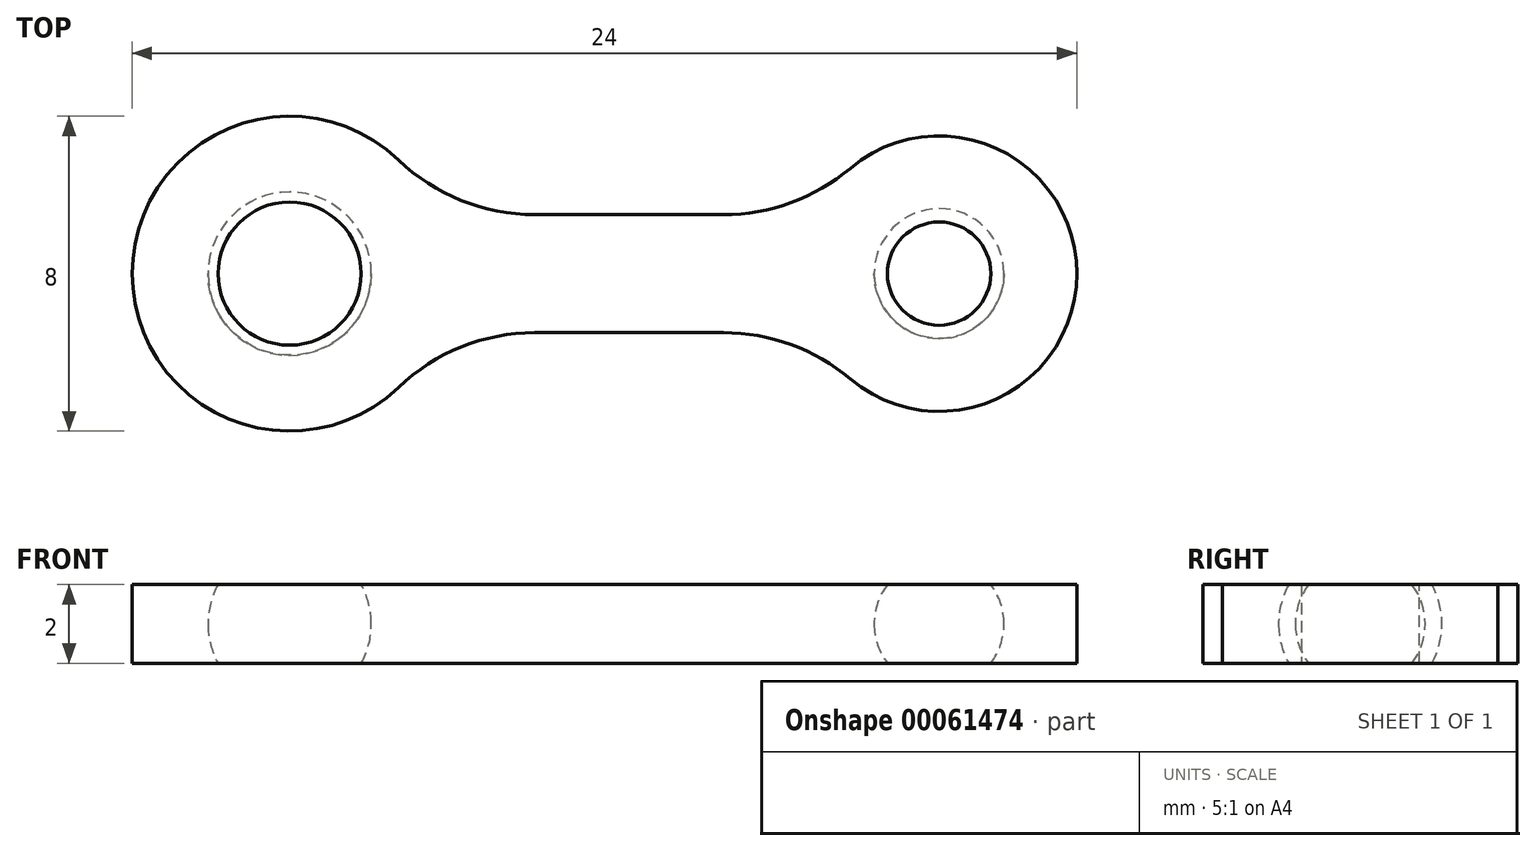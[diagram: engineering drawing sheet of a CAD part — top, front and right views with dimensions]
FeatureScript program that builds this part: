
annotation { "Feature Type Name" : "Feature", "Feature Type Description" : "" }
export const myFeature = defineFeature(function(context is Context, id is Id, definition is map)
    precondition{}
    {
        {
            var Q0;
            Q0=qCreatedBy(makeId("Top.planeOp"),FACE);
            var sketch = newSketch(context, id + "F0", { "sketchPlane" : qUnion([Q0])});
            skLineSegment(sketch, "E0.rect.bottom", {"start": v(5.09, -1.5) * mm, "end": v(-4.54, -1.5) * mm});
            skLineSegment(sketch, "E0.rect.top", {"start": v(5.09, 1.5) * mm, "end": v(-4.54, 1.5) * mm});
            skPoint(sketch, "E0.rect.middle", {"position": v(0, 0) * mm});
            skArc(sketch, "E1", {"start": v(-4.54, 1.5) * mm, "mid": v(-12.25, 0) * mm, "end": v(-4.54, -1.5) * mm});
            skArc(sketch, "E2", {"start": v(5.09, -1.5) * mm, "mid": v(11.75, 0) * mm, "end": v(5.09, 1.5) * mm});
            skPoint(sketch, "E3.orphan", {"position": v(-8.25, 1.5) * mm});
            skPoint(sketch, "E4.orphan", {"position": v(-8.25, -1.5) * mm});
            skPoint(sketch, "E5.orphan", {"position": v(8.25, 1.5) * mm});
            skPoint(sketch, "E6.orphan", {"position": v(8.25, -1.5) * mm});
            skArc(sketch, "E7", {"start": v(-10.33, 0) * mm, "mid": v(-8.25, -2.08) * mm, "end": v(-6.17, 0) * mm});
            skArc(sketch, "E8", {"start": v(6.6, 0) * mm, "mid": v(8.25, -1.65) * mm, "end": v(9.9, 0) * mm});
            skLineSegment(sketch, "E9", {"start": v(-10.33, 0) * mm, "end": v(-6.17, 0) * mm});
            skLineSegment(sketch, "E10", {"start": v(6.6, 0) * mm, "end": v(9.9, 0) * mm});
            skLineSegment(sketch, "E11", {"start": v(-18.85, 0) * mm, "end": v(25.97, 0) * mm, "construction": true});
            skPoint(sketch, "E11.endSnap0", {"position": v(-12.25, 0) * mm});
            skSolve(sketch);
        }
        {
            var Q0;
            Q0=makeQuery(id+"F0.imprint","IMPRINT",FACE,{"disambiguationData":[TD([[makeQuery(id+"F0.imprint","IMPRINT",EDGE,{"derivedFrom":sQuery(id+"F0.wireOp",EDGE,"E0.rect.bottom")}),-1.0]])]});
            var Q1;
            Q1=makeQuery(id+"F0.imprint","IMPRINT",FACE,{"disambiguationData":[TD([[makeQuery(id+"F0.imprint","IMPRINT",EDGE,{"derivedFrom":sQuery(id+"F0.wireOp",EDGE,"E7")}),1.0]])]});
            var Q2;
            Q2=makeQuery(id+"F0.imprint","IMPRINT",FACE,{"disambiguationData":[TD([[makeQuery(id+"F0.imprint","IMPRINT",EDGE,{"derivedFrom":sQuery(id+"F0.wireOp",EDGE,"E8")}),1.0]])]});
            extrude(context, id + "F1", {"entities" : qUnion([Q0, Q1, Q2]), "endBound" : BoundingType.SYMMETRIC, "depth" : 2 * mm});
        }
        {
            var Q0;
            Q0=makeQuery(id+"F0.imprint","IMPRINT",FACE,{"disambiguationData":[TD([[makeQuery(id+"F0.imprint","IMPRINT",EDGE,{"derivedFrom":sQuery(id+"F0.wireOp",EDGE,"E7")}),1.0]])]});
            var Q1;
            Q1=makeQuery(id+"F0.imprint","IMPRINT",FACE,{"disambiguationData":[TD([[makeQuery(id+"F0.imprint","IMPRINT",EDGE,{"derivedFrom":sQuery(id+"F0.wireOp",EDGE,"E8")}),1.0]])]});
            var Q2;
            Q2=sQuery(id+"F0.wireOp",EDGE,"E11");
            revolve(context, id + "F2", {"operationType" : NewBodyOperationType.REMOVE, "entities" : qUnion([Q0, Q1]), "axis" : qUnion([Q2]), "revolveType" : RevolveType.FULL});
        }
        {
            var Q0;
            Q0=makeQuery(id+"F1.opExtrude","SWEPT_EDGE",EDGE,{"disambiguationData":[OSD([sQuery(id+"F0.wireOp",EDGE,"E0.rect.top"),sQuery(id+"F0.wireOp",EDGE,"E1")])]});
            var Q1;
            Q1=makeQuery(id+"F1.opExtrude","SWEPT_EDGE",EDGE,{"disambiguationData":[OSD([sQuery(id+"F0.wireOp",EDGE,"E0.rect.top"),sQuery(id+"F0.wireOp",EDGE,"E2")])]});
            var Q2;
            Q2=makeQuery(id+"F1.opExtrude","SWEPT_EDGE",EDGE,{"disambiguationData":[OSD([sQuery(id+"F0.wireOp",EDGE,"E0.rect.bottom"),sQuery(id+"F0.wireOp",EDGE,"E1")])]});
            var Q3;
            Q3=makeQuery(id+"F1.opExtrude","SWEPT_EDGE",EDGE,{"disambiguationData":[OSD([sQuery(id+"F0.wireOp",EDGE,"E0.rect.bottom"),sQuery(id+"F0.wireOp",EDGE,"E2")])]});
            fillet(context, id + "F3", {"entities" : qUnion([Q0, Q1, Q2, Q3]), "radius" : 5 * mm, "tangentPropagation" : true, "allowEdgeOverflow" : false});
        }
    });
